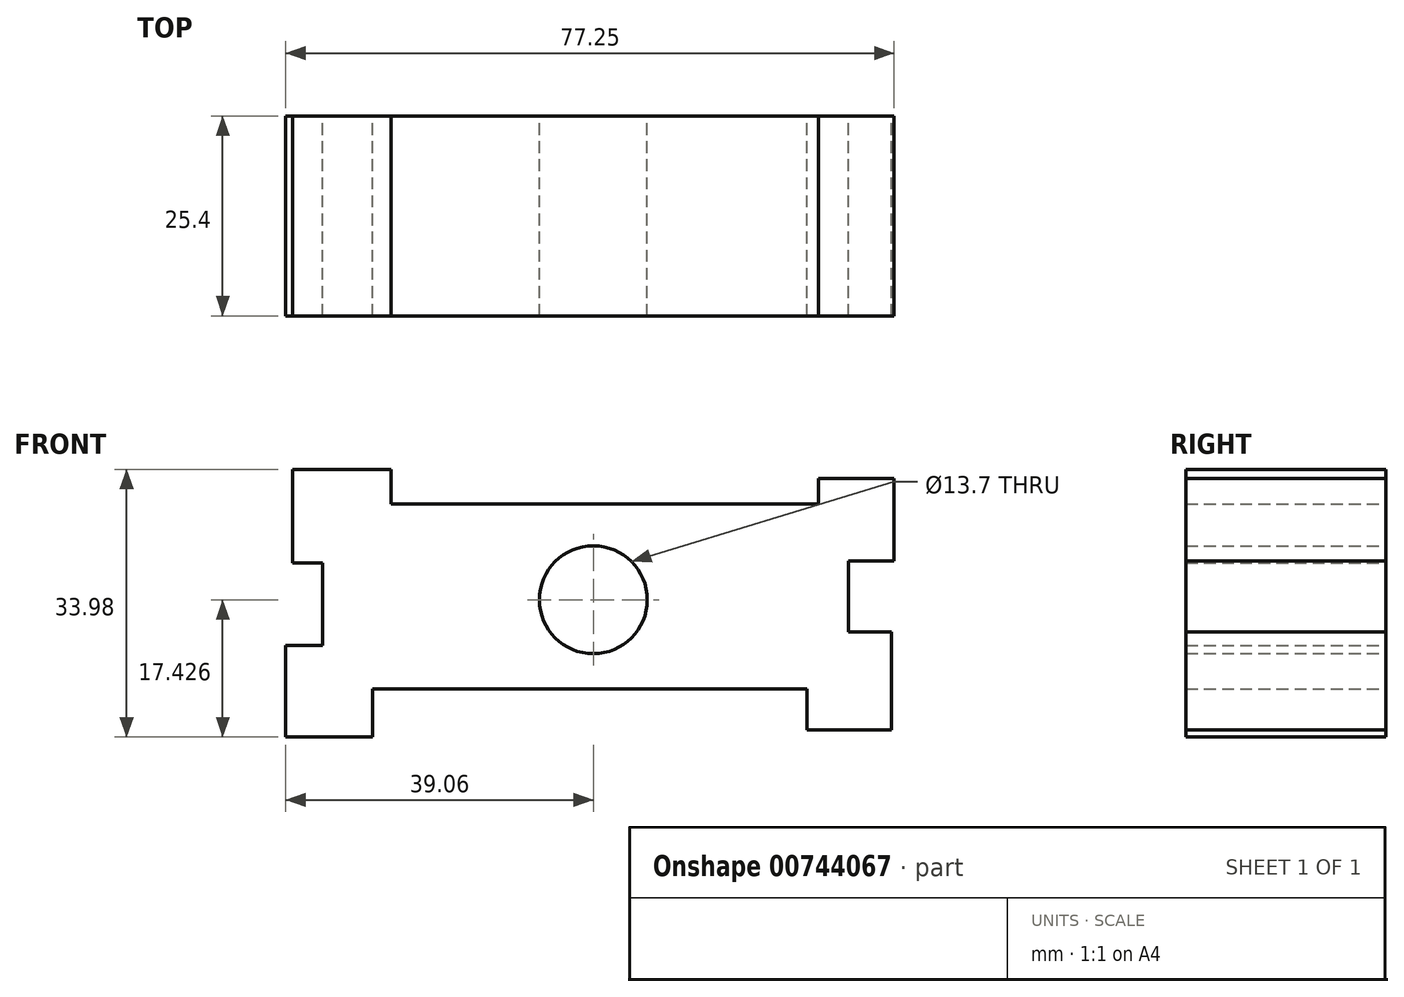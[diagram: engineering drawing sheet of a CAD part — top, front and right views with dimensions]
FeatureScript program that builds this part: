
annotation { "Feature Type Name" : "Feature", "Feature Type Description" : "" }
export const myFeature = defineFeature(function(context is Context, id is Id, definition is map)
    precondition{}
    {
        {
            var Q0;
            Q0=qCreatedBy(makeId("Front.planeOp"),FACE);
            var sketch = newSketch(context, id + "F0", { "sketchPlane" : qUnion([Q0])});
            skLineSegment(sketch, "E0.bottom", {"start": v(-34.41, 23.52) * mm, "end": v(32.38, 23.52) * mm});
            skLineSegment(sketch, "E0.top", {"start": v(-34.41, 0) * mm, "end": v(32.38, 0) * mm});
            skLineSegment(sketch, "E0.left", {"start": v(-34.41, 23.52) * mm, "end": v(-34.41, 0) * mm});
            skLineSegment(sketch, "E0.right", {"start": v(32.38, 23.52) * mm, "end": v(32.38, 0) * mm});
            skCircle(sketch, "E1", {"center": v(0, 11.33) * mm, "radius": 6.85 * mm});
            skLineSegment(sketch, "E2.bottom", {"start": v(-38.19, 27.88) * mm, "end": v(-25.7, 27.88) * mm});
            skLineSegment(sketch, "E2.top", {"start": v(-38.19, 15.97) * mm, "end": v(-25.7, 15.97) * mm});
            skLineSegment(sketch, "E2.left", {"start": v(-38.19, 27.88) * mm, "end": v(-38.19, 15.97) * mm});
            skLineSegment(sketch, "E2.right", {"start": v(-25.7, 27.88) * mm, "end": v(-25.7, 15.97) * mm});
            skLineSegment(sketch, "E3.bottom", {"start": v(28.6, 26.72) * mm, "end": v(38.19, 26.72) * mm});
            skLineSegment(sketch, "E3.top", {"start": v(28.6, 16.26) * mm, "end": v(38.19, 16.26) * mm});
            skLineSegment(sketch, "E3.left", {"start": v(28.6, 26.72) * mm, "end": v(28.6, 16.26) * mm});
            skLineSegment(sketch, "E3.right", {"start": v(38.19, 26.72) * mm, "end": v(38.19, 16.26) * mm});
            skLineSegment(sketch, "E4.bottom", {"start": v(27.15, 7.26) * mm, "end": v(37.9, 7.26) * mm});
            skLineSegment(sketch, "E4.top", {"start": v(27.15, -5.23) * mm, "end": v(37.9, -5.23) * mm});
            skLineSegment(sketch, "E4.left", {"start": v(27.15, 7.26) * mm, "end": v(27.15, -5.23) * mm});
            skLineSegment(sketch, "E4.right", {"start": v(37.9, 7.26) * mm, "end": v(37.9, -5.23) * mm});
            skLineSegment(sketch, "E5.bottom", {"start": v(-39.06, 5.52) * mm, "end": v(-28.03, 5.52) * mm});
            skLineSegment(sketch, "E5.top", {"start": v(-39.06, -6.1) * mm, "end": v(-28.03, -6.1) * mm});
            skLineSegment(sketch, "E5.left", {"start": v(-39.06, 5.52) * mm, "end": v(-39.06, -6.1) * mm});
            skLineSegment(sketch, "E5.right", {"start": v(-28.03, 5.52) * mm, "end": v(-28.03, -6.1) * mm});
            skSolve(sketch);
        }
        {
            var Q0;
            Q0=makeQuery(id+"F0.imprint","IMPRINT",FACE,{"disambiguationData":[TD([[makeQuery(id+"F0.imprint","IMPRINT",EDGE,{"derivedFrom":sQuery(id+"F0.wireOp",EDGE,"E0.bottom")}),-1.0]])]});
            extrude(context, id + "F1", {"entities" : qUnion([Q0]), "depth" : 25.4 * mm, "offsetDistance" : 25.4 * mm});
        }
        {
            var Q0;
            Q0 = qSketchRegion(id + "F0", true);
            extrude(context, id + "F2", {"entities" : qUnion([Q0]), "operationType" : NewBodyOperationType.ADD, "depth" : 25.4 * mm, "offsetDistance" : 25.4 * mm});
        }
    });
